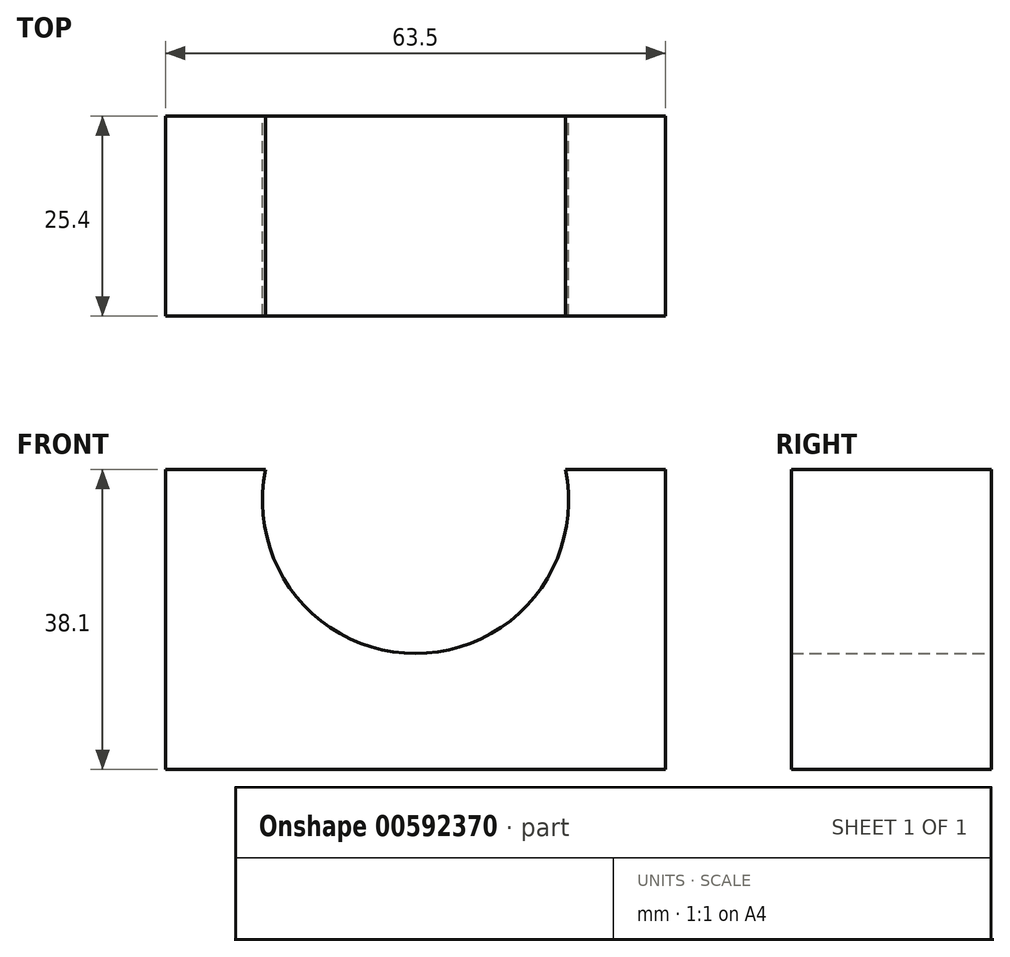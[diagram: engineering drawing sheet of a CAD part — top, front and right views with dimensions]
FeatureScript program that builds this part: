
annotation { "Feature Type Name" : "Feature", "Feature Type Description" : "" }
export const myFeature = defineFeature(function(context is Context, id is Id, definition is map)
    precondition{}
    {
        {
            var Q0;
            Q0=qCreatedBy(makeId("Front.planeOp"),FACE);
            var sketch = newSketch(context, id + "F0", { "sketchPlane" : qUnion([Q0])});
            skLineSegment(sketch, "E0", {"start": v(0, 0) * mm, "end": v(63.5, 0) * mm});
            skLineSegment(sketch, "E1", {"start": v(63.5, 0) * mm, "end": v(63.5, 38.1) * mm});
            skLineSegment(sketch, "E2", {"start": v(0, 0) * mm, "end": v(0, 38.1) * mm});
            skLineSegment(sketch, "E3", {"start": v(0, 38.1) * mm, "end": v(12.7, 38.1) * mm});
            skLineSegment(sketch, "E4", {"start": v(63.5, 38.1) * mm, "end": v(50.8, 38.1) * mm});
            skArc(sketch, "E5", {"start": v(12.7, 38.1) * mm, "mid": v(31.75, 14.73) * mm, "end": v(50.8, 38.1) * mm});
            skSolve(sketch);
        }
        {
            var Q0;
            Q0 = qSketchRegion(id + "F0", true);
            extrude(context, id + "F1", {"entities" : qUnion([Q0]), "depth" : 25.4 * mm, "offsetDistance" : 25.4 * mm});
        }
    });
